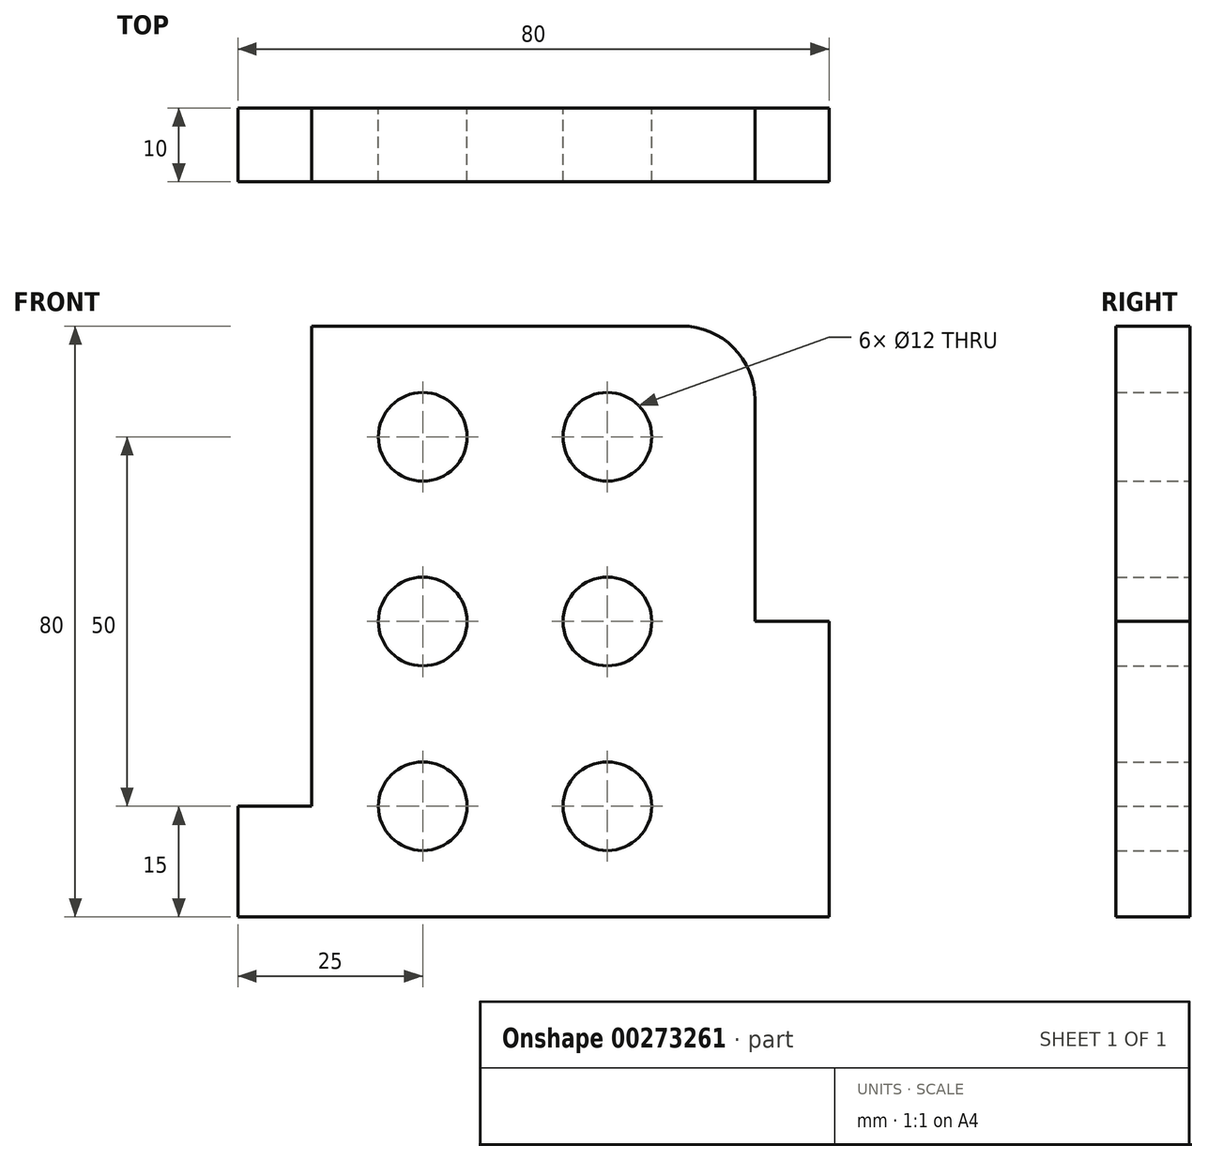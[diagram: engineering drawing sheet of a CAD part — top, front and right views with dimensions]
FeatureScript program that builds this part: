
annotation { "Feature Type Name" : "Feature", "Feature Type Description" : "" }
export const myFeature = defineFeature(function(context is Context, id is Id, definition is map)
    precondition{}
    {
        {
            var Q0;
            Q0=qCreatedBy(makeId("Front.planeOp"),FACE);
            var sketch = newSketch(context, id + "F0", { "sketchPlane" : qUnion([Q0])});
            skLineSegment(sketch, "E0", {"start": v(0, 0) * mm, "end": v(80, 0) * mm});
            skLineSegment(sketch, "E1", {"start": v(80, 0) * mm, "end": v(80, 40) * mm});
            skLineSegment(sketch, "E2", {"start": v(0, 0) * mm, "end": v(0, 15) * mm});
            skLineSegment(sketch, "E3", {"start": v(0, 15) * mm, "end": v(10, 15) * mm});
            skLineSegment(sketch, "E4", {"start": v(10, 15) * mm, "end": v(10, 80) * mm});
            skLineSegment(sketch, "E5", {"start": v(10, 80) * mm, "end": v(60, 80) * mm});
            skLineSegment(sketch, "E6", {"start": v(70, 70) * mm, "end": v(70, 40) * mm});
            skLineSegment(sketch, "E7", {"start": v(80, 40) * mm, "end": v(70, 40) * mm});
            skPoint(sketch, "E8.visualSharp", {"position": v(70, 80) * mm});
            skArc(sketch, "E8.filletArc", {"start": v(70, 70) * mm, "mid": v(67.07, 77.07) * mm, "end": v(60, 80) * mm});
            skCircle(sketch, "E9", {"center": v(25, 15) * mm, "radius": 6 * mm});
            skCircle(sketch, "E10.0.1.0", {"center": v(25, 40) * mm, "radius": 6 * mm});
            skCircle(sketch, "E10.0.2.0", {"center": v(25, 65) * mm, "radius": 6 * mm});
            skCircle(sketch, "E10.1.0.0", {"center": v(50, 15) * mm, "radius": 6 * mm});
            skCircle(sketch, "E10.1.1.0", {"center": v(50, 40) * mm, "radius": 6 * mm});
            skCircle(sketch, "E10.1.2.0", {"center": v(50, 65) * mm, "radius": 6 * mm});
            skLineSegment(sketch, "E10.direction1", {"start": v(25, 15) * mm, "end": v(50, 15) * mm, "construction": true});
            skLineSegment(sketch, "E10.direction2", {"start": v(25, 15) * mm, "end": v(25, 40) * mm, "construction": true});
            skSolve(sketch);
        }
        {
            var Q0;
            Q0=makeQuery(id+"F0.imprint","IMPRINT",FACE,{"disambiguationData":[TD([[makeQuery(id+"F0.imprint","IMPRINT",EDGE,{"derivedFrom":sQuery(id+"F0.wireOp",EDGE,"E0")}),1.0]])]});
            extrude(context, id + "F1", {"entities" : qUnion([Q0]), "depth" : 10 * mm});
        }
    });
